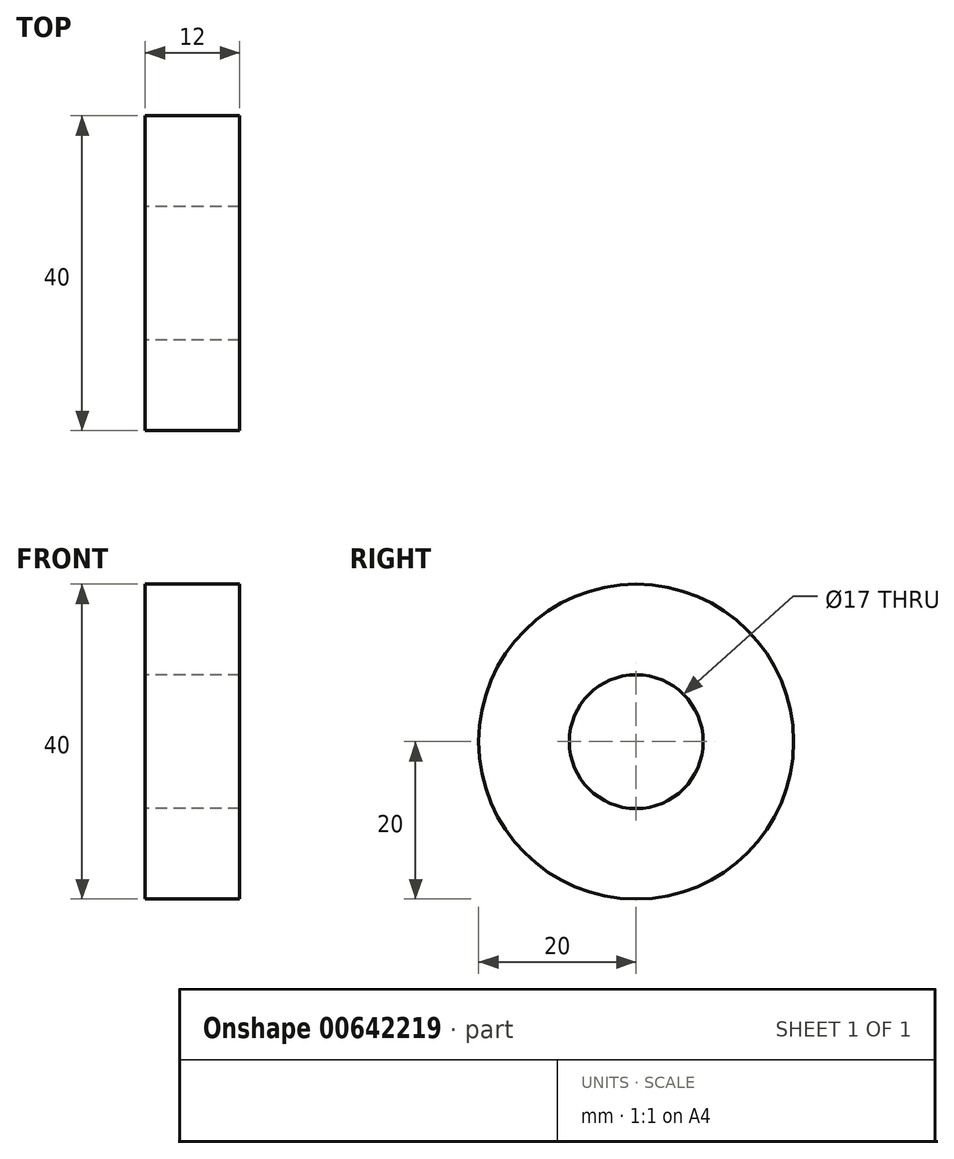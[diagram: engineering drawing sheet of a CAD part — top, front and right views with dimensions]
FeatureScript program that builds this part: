
annotation { "Feature Type Name" : "Feature", "Feature Type Description" : "" }
export const myFeature = defineFeature(function(context is Context, id is Id, definition is map)
    precondition{}
    {
        {
            var Q0;
            Q0=qCreatedBy(makeId("Front.planeOp"),FACE);
            var sketch = newSketch(context, id + "F0", { "sketchPlane" : qUnion([Q0])});
            skLineSegment(sketch, "E0.bottom", {"start": v(12, 8.5) * mm, "end": v(0, 8.5) * mm});
            skLineSegment(sketch, "E0.top", {"start": v(12, 20) * mm, "end": v(0, 20) * mm});
            skLineSegment(sketch, "E0.left", {"start": v(12, 8.5) * mm, "end": v(12, 20) * mm});
            skLineSegment(sketch, "E0.right", {"start": v(0, 8.5) * mm, "end": v(0, 20) * mm});
            skLineSegment(sketch, "E1", {"start": v(0, 0) * mm, "end": v(7.5, 0) * mm, "construction": true});
            skSolve(sketch);
        }
        {
            var Q0;
            Q0 = qSketchRegion(id + "F0", true);
            var Q1;
            Q1=sQuery(id+"F0.wireOp",EDGE,"E1");
            revolve(context, id + "F1", {"entities" : qUnion([Q0]), "axis" : qUnion([Q1]), "revolveType" : RevolveType.FULL});
        }
    });
